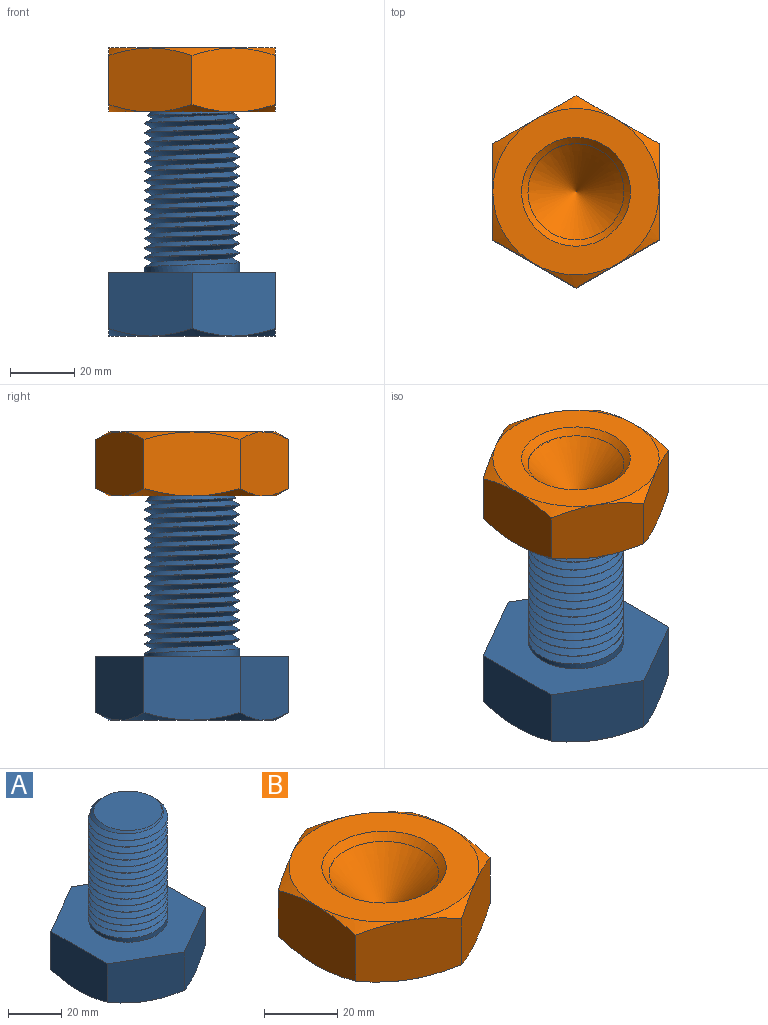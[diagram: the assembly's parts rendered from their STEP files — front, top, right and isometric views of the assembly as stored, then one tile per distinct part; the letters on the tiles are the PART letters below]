
ASSEMBLY  parts=2 mates=1
PART A: 21 faces, bbox 60x60x70.9 mm
  f0: cylinder r=14.88mm len=48mm, axis (0,0,-1), area 770mm2, adj f1,f8,f17,f19,f20
  f1: cone r=12.88mm half-angle=45deg, axis (0,0,-1), area 134mm2, adj f0,f16,f18,f20
  f2: plane 25.98x20.01mm, normal (0.5,-0.87,0), area 576.1mm2, adj f3,f7,f8,f9,f14
  f3: plane 30.02x20.01mm, normal (1,0,0), area 576.1mm2, adj f2,f4,f8,f13,f14
  f4: plane 25.98x20.01mm, normal (0.5,0.87,0), area 576.1mm2, adj f3,f5,f8,f12,f13
  f5: plane 25.98x20.01mm, normal (-0.5,0.87,0), area 576.1mm2, adj f4,f6,f8,f11,f12
  f6: plane 30.02x20.01mm, normal (-1,0,0), area 576.1mm2, adj f5,f7,f8,f10,f11
  f7: plane 25.98x20.01mm, normal (-0.5,-0.87,0), area 576.1mm2, adj f2,f6,f8,f9,f10
  f8: plane 60x51.96mm, normal (0,0,1), area 1643.1mm2, adj f0,f2,f3,f4,f5,f6,f7
  f9: cone r=41.51mm half-angle=60deg, axis (0,0,1), area 41.9mm2, adj f2,f7,f15
  f10: cone r=41.51mm half-angle=60deg, axis (0,0,1), area 41.9mm2, adj f6,f7,f15
  f11: cone r=41.51mm half-angle=60deg, axis (0,0,1), area 41.9mm2, adj f5,f6,f15
  f12: cone r=41.51mm half-angle=60deg, axis (0,0,1), area 41.9mm2, adj f4,f5,f15
  f13: cone r=41.51mm half-angle=60deg, axis (0,0,1), area 41.9mm2, adj f3,f4,f15
  f14: cone r=41.51mm half-angle=60deg, axis (0,0,1), area 41.9mm2, adj f2,f3,f15
  f15: plane 51.96x51.96mm, normal (0,0,-1), area 2120.6mm2, adj f9,f10,f11,f12,f13,f14
  f16: plane 25.75x25.75mm, normal (0,0,1), area 520.8mm2, adj f1
  f17: plane 2.9x2.51mm, normal (0,1,0), area 3.6mm2, adj f0,f19,f20
  f18: plane 2.51x1.84mm, normal (0,-1,0), area 1mm2, adj f1,f19,f20
  f19: bspline ~49.45x34.35mm, area 3984mm2, adj f0,f17,f18,f20
  f20: bspline ~49.45x34.35mm, area 3871.7mm2, adj f0,f1,f17,f18,f19
PART B: 28 faces, bbox 62.5x62.5x22.5 mm
  f0: cylinder r=15mm len=30mm, axis (0,0,-1), area 312.9mm2, adj f1,f2,f3,f4,f5,f6
  f1: bspline ~40.44x35.02mm, area 1294mm2, adj f0,f2,f4,f5
  f2: plane 2.91x1.88mm, normal (0.74,0.67,0), area 3.6mm2, adj f0,f1,f4
  f3: cone r=15mm half-angle=45deg, axis (0,0,1), area 999.6mm2, adj f0
  f4: bspline ~40.44x35.02mm, area 1294mm2, adj f0,f1,f2,f5
  f5: plane 2.9x2.51mm, normal (0,1,0), area 3.6mm2, adj f0,f1,f4
  f6: cone r=17mm half-angle=45deg, axis (0,0,-1), area 284.3mm2, adj f0,f7
  f7: plane 51.96x51.96mm, normal (0,0,-1), area 1212.7mm2, adj f6,f8,f23,f24,f25,f26,f27
  f8: cone r=37.16mm half-angle=60deg, axis (0,0,1), area 66.4mm2, adj f7,f9,f22
  f9: plane 28.44x22.48mm, normal (0.5,0.87,0), area 552.2mm2, adj f8,f10,f20,f21,f22,f27
  f10: cone r=37.16mm half-angle=60deg, axis (0,0,-1), area 66.4mm2, adj f9,f11,f22
  f11: plane 51.96x51.96mm, normal (0,0,1), area 1212.7mm2, adj f10,f12,f16,f17,f18,f19,f21
  f12: cone r=37.16mm half-angle=60deg, axis (0,0,-1), area 66.4mm2, adj f11,f13,f14
  f13: plane 28.44x22.48mm, normal (0.5,-0.87,0), area 552.2mm2, adj f12,f14,f18,f20,f25,f26
  f14: plane 28.44x22.48mm, normal (-0.5,-0.87,0), area 552.2mm2, adj f12,f13,f15,f16,f24,f25
  f15: plane 32.5x22.48mm, normal (-1,0,0), area 552.2mm2, adj f14,f16,f17,f22,f23,f24
  f16: cone r=37.16mm half-angle=60deg, axis (0,0,-1), area 66.4mm2, adj f11,f14,f15
  f17: cone r=37.16mm half-angle=60deg, axis (0,0,-1), area 66.4mm2, adj f11,f15,f22
  f18: cone r=37.16mm half-angle=60deg, axis (0,0,-1), area 66.4mm2, adj f11,f13,f20
  f19: cone r=15mm half-angle=45deg, axis (0,0,1), area 1284mm2, adj f11
  f20: plane 32.5x22.48mm, normal (1,0,0), area 552.2mm2, adj f9,f13,f18,f21,f26,f27
  f21: cone r=37.16mm half-angle=60deg, axis (0,0,-1), area 66.4mm2, adj f9,f11,f20
  f22: plane 28.44x22.48mm, normal (-0.5,0.87,0), area 552.2mm2, adj f8,f9,f10,f15,f17,f23
  f23: cone r=37.16mm half-angle=60deg, axis (0,0,1), area 66.4mm2, adj f7,f15,f22
  f24: cone r=37.16mm half-angle=60deg, axis (0,0,1), area 66.4mm2, adj f7,f14,f15
  f25: cone r=37.16mm half-angle=60deg, axis (0,0,1), area 66.4mm2, adj f7,f13,f14
  f26: cone r=37.16mm half-angle=60deg, axis (0,0,1), area 66.4mm2, adj f7,f13,f20
  f27: cone r=37.16mm half-angle=60deg, axis (0,0,1), area 66.4mm2, adj f7,f9,f20
PLACE A t=(2.94,-31.32,-84.98)mm
PLACE B t=(2.94,-31.32,-14.98)mm
MATE cylindrical B.f0 <-> A.f0  axis (0,0,-1) through (2.94,-31.32,-14.98)mm
